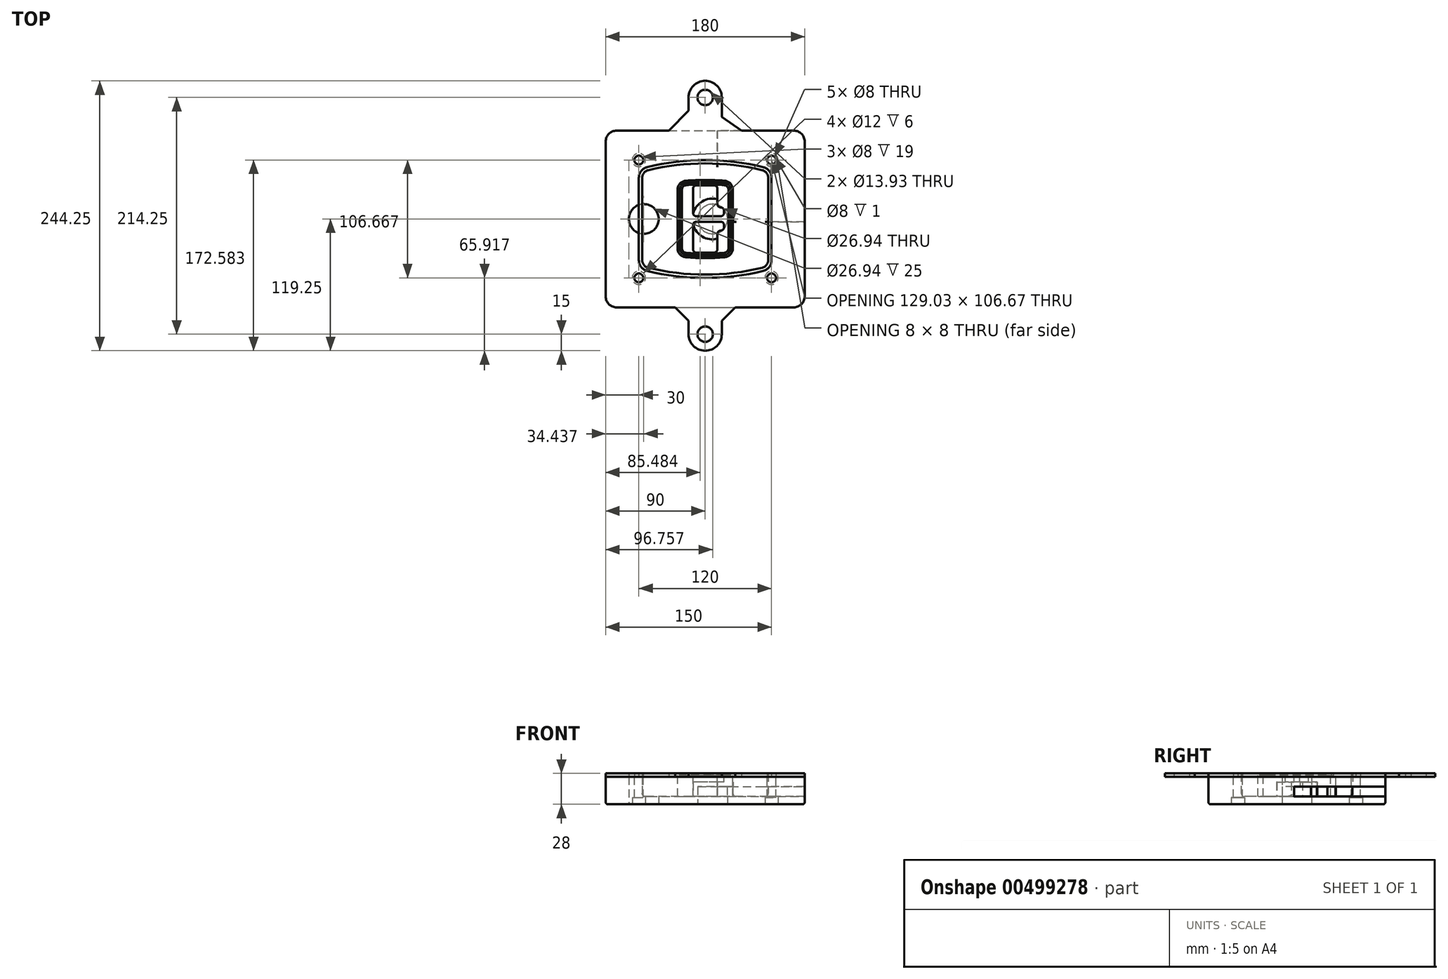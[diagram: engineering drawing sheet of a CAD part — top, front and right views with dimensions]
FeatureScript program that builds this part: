
annotation { "Feature Type Name" : "Feature", "Feature Type Description" : "" }
export const myFeature = defineFeature(function(context is Context, id is Id, definition is map)
    precondition{}
    {
        {
            var Q0;
            Q0=qCreatedBy(makeId("Top.planeOp"),FACE);
            var sketch = newSketch(context, id + "F0", { "sketchPlane" : qUnion([Q0])});
            skPoint(sketch, "E0.rect.middle", {"position": v(0, 0) * mm});
            skLineSegment(sketch, "E1.bottom", {"start": v(-80, -80) * mm, "end": v(80, -80) * mm});
            skLineSegment(sketch, "E1.top", {"start": v(-80, 80) * mm, "end": v(80, 80) * mm});
            skLineSegment(sketch, "E1.left", {"start": v(-90, -70) * mm, "end": v(-90, 70) * mm});
            skLineSegment(sketch, "E1.right", {"start": v(90, -70) * mm, "end": v(90, 70) * mm});
            skLineSegment(sketch, "E2", {"start": v(-90, 80) * mm, "end": v(90, -80) * mm, "construction": true});
            skLineSegment(sketch, "E3", {"start": v(90, 80) * mm, "end": v(-90, -80) * mm, "construction": true});
            skCircle(sketch, "E4", {"center": v(-60, 53.33) * mm, "radius": 4 * mm});
            skCircle(sketch, "E5", {"center": v(60, 53.33) * mm, "radius": 4 * mm});
            skCircle(sketch, "E6", {"center": v(60, -53.33) * mm, "radius": 4 * mm});
            skCircle(sketch, "E7", {"center": v(-60, -53.33) * mm, "radius": 4 * mm});
            skLineSegment(sketch, "E8", {"start": v(-60, 53.33) * mm, "end": v(60, 53.33) * mm, "construction": true});
            skLineSegment(sketch, "E9", {"start": v(60, 53.33) * mm, "end": v(60, -53.33) * mm, "construction": true});
            skLineSegment(sketch, "E10", {"start": v(60, -53.33) * mm, "end": v(-60, -53.33) * mm, "construction": true});
            skLineSegment(sketch, "E11", {"start": v(-60, -53.33) * mm, "end": v(-60, 53.33) * mm, "construction": true});
            skLineSegment(sketch, "E12", {"start": v(-60, 37.3) * mm, "end": v(-60, -37.3) * mm});
            skLineSegment(sketch, "E13", {"start": v(60, 37.3) * mm, "end": v(60, -37.3) * mm});
            skArc(sketch, "E14", {"start": v(52.38, 47.01) * mm, "mid": v(0, 53.33) * mm, "end": v(-52.38, 47.01) * mm});
            skArc(sketch, "E15", {"start": v(-52.38, -47.01) * mm, "mid": v(0, -53.33) * mm, "end": v(52.38, -47.01) * mm});
            skLineSegment(sketch, "E16", {"start": v(-60, 0) * mm, "end": v(60, 0) * mm, "construction": true});
            skPoint(sketch, "E17.visualSharp", {"position": v(-60, -45) * mm});
            skArc(sketch, "E17.filletArc", {"start": v(-60, -37.3) * mm, "mid": v(-57.87, -43.47) * mm, "end": v(-52.38, -47.01) * mm});
            skPoint(sketch, "E18.visualSharp", {"position": v(-60, 45) * mm});
            skArc(sketch, "E18.filletArc", {"start": v(-52.38, 47.01) * mm, "mid": v(-57.87, 43.47) * mm, "end": v(-60, 37.3) * mm});
            skPoint(sketch, "E19.visualSharp", {"position": v(60, 45) * mm});
            skArc(sketch, "E19.filletArc", {"start": v(60, 37.3) * mm, "mid": v(57.87, 43.47) * mm, "end": v(52.38, 47.01) * mm});
            skPoint(sketch, "E20.visualSharp", {"position": v(60, -45) * mm});
            skArc(sketch, "E20.filletArc", {"start": v(52.38, -47.01) * mm, "mid": v(57.87, -43.47) * mm, "end": v(60, -37.3) * mm});
            skPoint(sketch, "E21.visualSharp", {"position": v(-90, 80) * mm});
            skArc(sketch, "E21.filletArc", {"start": v(-80, 80) * mm, "mid": v(-87.07, 77.07) * mm, "end": v(-90, 70) * mm});
            skPoint(sketch, "E22.visualSharp", {"position": v(90, 80) * mm});
            skArc(sketch, "E22.filletArc", {"start": v(90, 70) * mm, "mid": v(87.07, 77.07) * mm, "end": v(80, 80) * mm});
            skPoint(sketch, "E23.visualSharp", {"position": v(90, -80) * mm});
            skArc(sketch, "E23.filletArc", {"start": v(80, -80) * mm, "mid": v(87.07, -77.07) * mm, "end": v(90, -70) * mm});
            skPoint(sketch, "E24.visualSharp", {"position": v(-90, -80) * mm});
            skArc(sketch, "E24.filletArc", {"start": v(-90, -70) * mm, "mid": v(-87.07, -77.07) * mm, "end": v(-80, -80) * mm});
            skArc(sketch, "E25.0", {"start": v(57, 37.3) * mm, "mid": v(55.5, 41.62) * mm, "end": v(51.67, 44.1) * mm});
            skLineSegment(sketch, "E25.1", {"start": v(57, 37.3) * mm, "end": v(57, -37.3) * mm});
            skArc(sketch, "E25.2", {"start": v(51.67, -44.1) * mm, "mid": v(55.5, -41.62) * mm, "end": v(57, -37.3) * mm});
            skArc(sketch, "E25.3", {"start": v(-51.67, -44.1) * mm, "mid": v(0, -50.33) * mm, "end": v(51.67, -44.1) * mm});
            skArc(sketch, "E25.4", {"start": v(-57, -37.3) * mm, "mid": v(-55.5, -41.62) * mm, "end": v(-51.67, -44.1) * mm});
            skArc(sketch, "E25.5", {"start": v(51.67, 44.1) * mm, "mid": v(0, 50.33) * mm, "end": v(-51.67, 44.1) * mm});
            skLineSegment(sketch, "E25.6", {"start": v(-57, 37.3) * mm, "end": v(-57, -37.3) * mm});
            skArc(sketch, "E25.7", {"start": v(-51.67, 44.1) * mm, "mid": v(-55.5, 41.62) * mm, "end": v(-57, 37.3) * mm});
            skArc(sketch, "E26.0", {"start": v(-53.33, 50.9) * mm, "mid": v(-61.01, 45.94) * mm, "end": v(-64, 37.3) * mm});
            skArc(sketch, "E26.1", {"start": v(53.33, 50.9) * mm, "mid": v(0, 57.33) * mm, "end": v(-53.33, 50.9) * mm});
            skArc(sketch, "E26.2", {"start": v(64, 37.3) * mm, "mid": v(61.01, 45.94) * mm, "end": v(53.33, 50.9) * mm});
            skLineSegment(sketch, "E26.3", {"start": v(64, 37.3) * mm, "end": v(64, -37.3) * mm});
            skArc(sketch, "E26.4", {"start": v(53.33, -50.9) * mm, "mid": v(61.01, -45.94) * mm, "end": v(64, -37.3) * mm});
            skLineSegment(sketch, "E26.5", {"start": v(-64, 37.3) * mm, "end": v(-64, -37.3) * mm});
            skArc(sketch, "E26.6", {"start": v(-53.33, -50.9) * mm, "mid": v(0, -57.33) * mm, "end": v(53.33, -50.9) * mm});
            skArc(sketch, "E26.7", {"start": v(-64, -37.3) * mm, "mid": v(-61.01, -45.94) * mm, "end": v(-53.33, -50.9) * mm});
            skSolve(sketch);
        }
        {
            var Q0;
            Q0=makeQuery(id+"F0.imprint","IMPRINT",FACE,{"disambiguationData":[TD([[makeQuery(id+"F0.imprint","IMPRINT",EDGE,{"derivedFrom":sQuery(id+"F0.wireOp",EDGE,"E1.bottom")}),1.0]])]});
            var Q1;
            Q1=makeQuery(id+"F0.imprint","IMPRINT",FACE,{"disambiguationData":[TD([[makeQuery(id+"F0.imprint","IMPRINT",EDGE,{"derivedFrom":sQuery(id+"F0.wireOp",EDGE,"E12")}),1.0]])]});
            var Q2;
            Q2=makeQuery(id+"F0.imprint","IMPRINT",FACE,{"disambiguationData":[TD([[makeQuery(id+"F0.imprint","IMPRINT",EDGE,{"derivedFrom":sQuery(id+"F0.wireOp",EDGE,"E25.0")}),1.0]])]});
            var Q3;
            Q3=makeQuery(id+"F0.imprint","IMPRINT",FACE,{"disambiguationData":[TD([[makeQuery(id+"F0.imprint","IMPRINT",EDGE,{"derivedFrom":sQuery(id+"F0.wireOp",EDGE,"E12")}),-1.0]])]});
            extrude(context, id + "F1", {"entities" : qUnion([Q0, Q1, Q2, Q3]), "oppositeDirection" : true, "depth" : 25 * mm});
        }
        {
            var Q0;
            Q0=makeQuery(id+"F0.imprint","IMPRINT",FACE,{"disambiguationData":[TD([[makeQuery(id+"F0.imprint","IMPRINT",EDGE,{"derivedFrom":sQuery(id+"F0.wireOp",EDGE,"E12")}),1.0]])]});
            extrude(context, id + "F2", {"entities" : qUnion([Q0]), "operationType" : NewBodyOperationType.ADD, "depth" : 3 * mm});
        }
        {
            var Q0;
            Q0=makeQuery(id+"F0.imprint","IMPRINT",FACE,{"disambiguationData":[TD([[makeQuery(id+"F0.imprint","IMPRINT",EDGE,{"derivedFrom":sQuery(id+"F0.wireOp",EDGE,"E25.0")}),1.0]])]});
            extrude(context, id + "F3", {"entities" : qUnion([Q0]), "operationType" : NewBodyOperationType.REMOVE, "oppositeDirection" : true, "depth" : 18 * mm});
        }
        {
            var Q0;
            Q0=makeQuery(id+"F2.opExtrude","CAP_FACE",FACE,{"disambiguationData":[OSD([sQuery(id+"F0.wireOp",EDGE,"E12"),sQuery(id+"F0.wireOp",EDGE,"E13"),sQuery(id+"F0.wireOp",EDGE,"E14"),sQuery(id+"F0.wireOp",EDGE,"E15"),sQuery(id+"F0.wireOp",EDGE,"E17.filletArc"),sQuery(id+"F0.wireOp",EDGE,"E18.filletArc"),sQuery(id+"F0.wireOp",EDGE,"E19.filletArc"),sQuery(id+"F0.wireOp",EDGE,"E20.filletArc"),sQuery(id+"F0.wireOp",EDGE,"E25.0"),sQuery(id+"F0.wireOp",EDGE,"E25.1"),sQuery(id+"F0.wireOp",EDGE,"E25.2"),sQuery(id+"F0.wireOp",EDGE,"E25.3"),sQuery(id+"F0.wireOp",EDGE,"E25.4"),sQuery(id+"F0.wireOp",EDGE,"E25.5"),sQuery(id+"F0.wireOp",EDGE,"E25.6"),sQuery(id+"F0.wireOp",EDGE,"E25.7")])],"isStart":false});
            var sketch = newSketch(context, id + "F4", { "sketchPlane" : qUnion([Q0])});
            skArc(sketch, "E27.0", {"start": v(-17.7, -34.56) * mm, "mid": v(0, -35.33) * mm, "end": v(17.7, -34.56) * mm});
            skArc(sketch, "E28.0", {"start": v(17.7, 34.56) * mm, "mid": v(0, 35.33) * mm, "end": v(-17.7, 34.56) * mm});
            skLineSegment(sketch, "E29", {"start": v(-25, 26.59) * mm, "end": v(-25, -26.59) * mm});
            skLineSegment(sketch, "E30", {"start": v(25, 26.59) * mm, "end": v(25, -26.59) * mm});
            skLineSegment(sketch, "E31", {"start": v(-25, 33.78) * mm, "end": v(25, 33.78) * mm, "construction": true});
            skLineSegment(sketch, "E32", {"start": v(-25, -33.78) * mm, "end": v(25, -33.78) * mm, "construction": true});
            skPoint(sketch, "E33.visualSharp", {"position": v(-25, 33.78) * mm});
            skArc(sketch, "E33.filletArc", {"start": v(-17.7, 34.56) * mm, "mid": v(-22.9, 32) * mm, "end": v(-25, 26.59) * mm});
            skPoint(sketch, "E34.visualSharp", {"position": v(25, 33.78) * mm});
            skArc(sketch, "E34.filletArc", {"start": v(25, 26.59) * mm, "mid": v(22.9, 32) * mm, "end": v(17.7, 34.56) * mm});
            skPoint(sketch, "E35.visualSharp", {"position": v(25, -33.78) * mm});
            skArc(sketch, "E35.filletArc", {"start": v(17.7, -34.56) * mm, "mid": v(22.9, -32) * mm, "end": v(25, -26.59) * mm});
            skPoint(sketch, "E36.visualSharp", {"position": v(-25, -33.78) * mm});
            skArc(sketch, "E36.filletArc", {"start": v(-25, -26.59) * mm, "mid": v(-22.9, -32) * mm, "end": v(-17.7, -34.56) * mm});
            skArc(sketch, "E37.0", {"start": v(51.67, 44.1) * mm, "mid": v(0, 50.33) * mm, "end": v(-51.67, 44.1) * mm});
            skArc(sketch, "E37.1", {"start": v(-51.67, 44.1) * mm, "mid": v(-55.5, 41.62) * mm, "end": v(-57, 37.3) * mm});
            skLineSegment(sketch, "E37.2", {"start": v(-57, 37.3) * mm, "end": v(-57, -37.3) * mm});
            skArc(sketch, "E37.3", {"start": v(-57, -37.3) * mm, "mid": v(-55.5, -41.62) * mm, "end": v(-51.67, -44.1) * mm});
            skArc(sketch, "E37.4", {"start": v(-51.67, -44.1) * mm, "mid": v(0, -50.33) * mm, "end": v(51.67, -44.1) * mm});
            skArc(sketch, "E37.5", {"start": v(51.67, -44.1) * mm, "mid": v(55.5, -41.62) * mm, "end": v(57, -37.3) * mm});
            skLineSegment(sketch, "E37.6", {"start": v(57, 37.3) * mm, "end": v(57, -37.3) * mm});
            skArc(sketch, "E37.7", {"start": v(57, 37.3) * mm, "mid": v(55.5, 41.62) * mm, "end": v(51.67, 44.1) * mm});
            skLineSegment(sketch, "E38.0", {"start": v(23, 26.59) * mm, "end": v(23, -26.59) * mm});
            skArc(sketch, "E38.1", {"start": v(17.53, -32.56) * mm, "mid": v(21.42, -30.64) * mm, "end": v(23, -26.59) * mm});
            skArc(sketch, "E38.2", {"start": v(-17.53, -32.56) * mm, "mid": v(0, -33.33) * mm, "end": v(17.53, -32.56) * mm});
            skArc(sketch, "E38.3", {"start": v(-23, -26.59) * mm, "mid": v(-21.42, -30.64) * mm, "end": v(-17.53, -32.56) * mm});
            skLineSegment(sketch, "E38.4", {"start": v(-23, 26.59) * mm, "end": v(-23, -26.59) * mm});
            skArc(sketch, "E38.5", {"start": v(23, 26.59) * mm, "mid": v(21.42, 30.64) * mm, "end": v(17.53, 32.56) * mm});
            skArc(sketch, "E38.6", {"start": v(-17.53, 32.56) * mm, "mid": v(-21.42, 30.64) * mm, "end": v(-23, 26.59) * mm});
            skArc(sketch, "E38.7", {"start": v(17.53, 32.56) * mm, "mid": v(0, 33.33) * mm, "end": v(-17.53, 32.56) * mm});
            skArc(sketch, "E39.0", {"start": v(21, 26.59) * mm, "mid": v(19.95, 29.29) * mm, "end": v(17.35, 30.57) * mm});
            skLineSegment(sketch, "E39.1", {"start": v(21, 26.59) * mm, "end": v(21, -26.59) * mm});
            skArc(sketch, "E39.2", {"start": v(17.35, -30.57) * mm, "mid": v(19.95, -29.29) * mm, "end": v(21, -26.59) * mm});
            skArc(sketch, "E39.3", {"start": v(-17.35, -30.57) * mm, "mid": v(0, -31.33) * mm, "end": v(17.35, -30.57) * mm});
            skArc(sketch, "E39.4", {"start": v(-21, -26.59) * mm, "mid": v(-19.95, -29.29) * mm, "end": v(-17.35, -30.57) * mm});
            skArc(sketch, "E39.5", {"start": v(17.35, 30.57) * mm, "mid": v(0, 31.33) * mm, "end": v(-17.35, 30.57) * mm});
            skLineSegment(sketch, "E39.6", {"start": v(-21, 26.59) * mm, "end": v(-21, -26.59) * mm});
            skArc(sketch, "E39.7", {"start": v(-17.35, 30.57) * mm, "mid": v(-19.95, 29.29) * mm, "end": v(-21, 26.59) * mm});
            skLineSegment(sketch, "E40", {"start": v(-25, 0) * mm, "end": v(25, 0) * mm, "construction": true});
            skLineSegment(sketch, "E41", {"start": v(-11, 5.5) * mm, "end": v(-11, 27.5) * mm});
            skLineSegment(sketch, "E42", {"start": v(-8, 30.5) * mm, "end": v(8, 30.5) * mm});
            skLineSegment(sketch, "E43", {"start": v(11, 27.5) * mm, "end": v(11, 13.5) * mm});
            skLineSegment(sketch, "E44", {"start": v(14, 10.5) * mm, "end": v(14, 10.5) * mm});
            skLineSegment(sketch, "E45", {"start": v(17, 7.5) * mm, "end": v(17, 5.5) * mm});
            skLineSegment(sketch, "E46", {"start": v(14, 2.5) * mm, "end": v(-8, 2.5) * mm});
            skPoint(sketch, "E47.visualSharp", {"position": v(-11, 30.5) * mm});
            skArc(sketch, "E47.filletArc", {"start": v(-8, 30.5) * mm, "mid": v(-10.12, 29.62) * mm, "end": v(-11, 27.5) * mm});
            skPoint(sketch, "E48.visualSharp", {"position": v(11, 30.5) * mm});
            skArc(sketch, "E48.filletArc", {"start": v(11, 27.5) * mm, "mid": v(10.12, 29.62) * mm, "end": v(8, 30.5) * mm});
            skPoint(sketch, "E49.visualSharp", {"position": v(11, 10.5) * mm});
            skArc(sketch, "E49.filletArc", {"start": v(11, 13.5) * mm, "mid": v(11.88, 11.38) * mm, "end": v(14, 10.5) * mm});
            skPoint(sketch, "E50.visualSharp", {"position": v(17, 10.5) * mm});
            skArc(sketch, "E50.filletArc", {"start": v(17, 7.5) * mm, "mid": v(16.12, 9.62) * mm, "end": v(14, 10.5) * mm});
            skPoint(sketch, "E51.visualSharp", {"position": v(17, 2.5) * mm});
            skArc(sketch, "E51.filletArc", {"start": v(14, 2.5) * mm, "mid": v(16.12, 3.38) * mm, "end": v(17, 5.5) * mm});
            skPoint(sketch, "E52.visualSharp", {"position": v(-11, 2.5) * mm});
            skArc(sketch, "E52.filletArc", {"start": v(-11, 5.5) * mm, "mid": v(-10.12, 3.38) * mm, "end": v(-8, 2.5) * mm});
            skLineSegment(sketch, "E53.0.MirrorCS", {"start": v(14, -2.5) * mm, "end": v(-8, -2.5) * mm});
            skArc(sketch, "E54.0.MirrorCS", {"start": v(-11, -5.5) * mm, "mid": v(-10.12, -3.38) * mm, "end": v(-8, -2.5) * mm});
            skLineSegment(sketch, "E55.0.MirrorCS", {"start": v(-11, -5.5) * mm, "end": v(-11, -27.5) * mm});
            skArc(sketch, "E56.0.MirrorCS", {"start": v(-8, -30.5) * mm, "mid": v(-10.12, -29.62) * mm, "end": v(-11, -27.5) * mm});
            skLineSegment(sketch, "E57.0.MirrorCS", {"start": v(-8, -30.5) * mm, "end": v(8, -30.5) * mm});
            skArc(sketch, "E58.0.MirrorCS", {"start": v(11, -27.5) * mm, "mid": v(10.12, -29.62) * mm, "end": v(8, -30.5) * mm});
            skLineSegment(sketch, "E59.0.MirrorCS", {"start": v(11, -27.5) * mm, "end": v(11, -13.5) * mm});
            skArc(sketch, "E60.0.MirrorCS", {"start": v(11, -13.5) * mm, "mid": v(11.88, -11.38) * mm, "end": v(14, -10.5) * mm});
            skArc(sketch, "E61.0.MirrorCS", {"start": v(17, -7.5) * mm, "mid": v(16.12, -9.62) * mm, "end": v(14, -10.5) * mm});
            skLineSegment(sketch, "E62.0.MirrorCS", {"start": v(17, -7.5) * mm, "end": v(17, -5.5) * mm});
            skArc(sketch, "E63.0.MirrorCS", {"start": v(14, -2.5) * mm, "mid": v(16.12, -3.38) * mm, "end": v(17, -5.5) * mm});
            skSolve(sketch);
        }
        {
            var Q0;
            Q0=makeQuery(id+"F4.imprint","IMPRINT",FACE,{"disambiguationData":[TD([[makeQuery(id+"F4.imprint","IMPRINT",EDGE,{"derivedFrom":sQuery(id+"F4.wireOp",EDGE,"E27.0")}),1.0]])]});
            var Q1;
            Q1=makeQuery(id+"F4.imprint","IMPRINT",FACE,{"disambiguationData":[TD([[makeQuery(id+"F4.imprint","IMPRINT",EDGE,{"derivedFrom":sQuery(id+"F4.wireOp",EDGE,"E38.0")}),-1.0]])]});
            var Q2;
            Q2=makeQuery(id+"F4.imprint","IMPRINT",FACE,{"disambiguationData":[TD([[makeQuery(id+"F4.imprint","IMPRINT",EDGE,{"derivedFrom":sQuery(id+"F4.wireOp",EDGE,"E39.0")}),1.0]])]});
            extrude(context, id + "F5", {"entities" : qUnion([Q0, Q1, Q2]), "operationType" : NewBodyOperationType.ADD, "endBound" : BoundingType.UP_TO_NEXT, "oppositeDirection" : true, "depth" : 25 * mm});
        }
        {
            var Q0;
            Q0=makeQuery(id+"F4.imprint","IMPRINT",FACE,{"disambiguationData":[TD([[makeQuery(id+"F4.imprint","IMPRINT",EDGE,{"derivedFrom":sQuery(id+"F4.wireOp",EDGE,"E38.0")}),-1.0]])]});
            extrude(context, id + "F6", {"entities" : qUnion([Q0]), "operationType" : NewBodyOperationType.REMOVE, "oppositeDirection" : true, "depth" : 2 * mm});
        }
        {
            var Q0;
            Q0=makeQuery(id+"F1.opExtrude","CAP_FACE",FACE,{"disambiguationData":[OSD([sQuery(id+"F0.wireOp",EDGE,"E1.bottom"),sQuery(id+"F0.wireOp",EDGE,"E1.top"),sQuery(id+"F0.wireOp",EDGE,"E1.left"),sQuery(id+"F0.wireOp",EDGE,"E1.right"),sQuery(id+"F0.wireOp",EDGE,"E4"),sQuery(id+"F0.wireOp",EDGE,"E5"),sQuery(id+"F0.wireOp",EDGE,"E6"),sQuery(id+"F0.wireOp",EDGE,"E7"),sQuery(id+"F0.wireOp",EDGE,"E21.filletArc"),sQuery(id+"F0.wireOp",EDGE,"E22.filletArc"),sQuery(id+"F0.wireOp",EDGE,"E23.filletArc"),sQuery(id+"F0.wireOp",EDGE,"E24.filletArc")])],"isStart":false});
            var sketch = newSketch(context, id + "F7", { "sketchPlane" : qUnion([Q0])});
            skCircle(sketch, "E64", {"center": v(6.76, 0) * mm, "radius": 13.47 * mm});
            skCircle(sketch, "E65", {"center": v(-55.56, 0) * mm, "radius": 13.47 * mm});
            skLineSegment(sketch, "E66", {"start": v(90, 0) * mm, "end": v(-90, 0) * mm});
            skCircle(sketch, "E67", {"center": v(6.76, 0) * mm, "radius": 18.47 * mm});
            skCircle(sketch, "E68", {"center": v(60, -53.33) * mm, "radius": 6 * mm});
            skCircle(sketch, "E69", {"center": v(-60, -53.33) * mm, "radius": 6 * mm});
            skCircle(sketch, "E70", {"center": v(-60, 53.33) * mm, "radius": 6 * mm});
            skCircle(sketch, "E71", {"center": v(60, 53.33) * mm, "radius": 6 * mm});
            skSolve(sketch);
        }
        {
            var Q0;
            {var subQ1=sQuery(id+"F7.wireOp",EDGE,"E66");var subQ4=sQuery(id+"F7.wireOp",EDGE,"E64");var subQ6=makeQuery(id+"F7.imprint","INTERSECT",VERTEX,{"disambiguationData":[OD(0.0)],"derivedFrom":[subQ4,subQ1]});Q0=makeQuery(id+"F7.imprint","IMPRINT",FACE,{"disambiguationData":[TD([[makeQuery(id+"F7.imprint","IMPRINT",EDGE,{"disambiguationData":[TD([[subQ6,-1.0]])],"derivedFrom":subQ4}),-1.0]])]});}
            var Q1;
            {var subQ0=sQuery(id+"F7.wireOp",EDGE,"E66");var subQ1=sQuery(id+"F7.wireOp",EDGE,"E64");var subQ3=makeQuery(id+"F7.imprint","INTERSECT",VERTEX,{"disambiguationData":[OD(0.0)],"derivedFrom":[subQ1,subQ0]});Q1=makeQuery(id+"F7.imprint","IMPRINT",FACE,{"disambiguationData":[TD([[makeQuery(id+"F7.imprint","IMPRINT",EDGE,{"disambiguationData":[TD([[subQ3,-1.0]])],"derivedFrom":subQ1}),1.0]])]});}
            var Q2;
            {var subQ0=sQuery(id+"F7.wireOp",EDGE,"E66");var subQ1=sQuery(id+"F7.wireOp",EDGE,"E64");var subQ3=makeQuery(id+"F7.imprint","INTERSECT",VERTEX,{"disambiguationData":[OD(0.0)],"derivedFrom":[subQ1,subQ0]});Q2=makeQuery(id+"F7.imprint","IMPRINT",FACE,{"disambiguationData":[TD([[makeQuery(id+"F7.imprint","IMPRINT",EDGE,{"disambiguationData":[TD([[subQ3,1.0]])],"derivedFrom":subQ1}),1.0]])]});}
            var Q3;
            {var subQ1=sQuery(id+"F7.wireOp",EDGE,"E66");var subQ4=sQuery(id+"F7.wireOp",EDGE,"E64");var subQ6=makeQuery(id+"F7.imprint","INTERSECT",VERTEX,{"disambiguationData":[OD(0.0)],"derivedFrom":[subQ4,subQ1]});Q3=makeQuery(id+"F7.imprint","IMPRINT",FACE,{"disambiguationData":[TD([[makeQuery(id+"F7.imprint","IMPRINT",EDGE,{"disambiguationData":[TD([[subQ6,1.0]])],"derivedFrom":subQ4}),-1.0]])]});}
            extrude(context, id + "F8", {"entities" : qUnion([Q0, Q1, Q2, Q3]), "operationType" : NewBodyOperationType.ADD, "oppositeDirection" : true, "depth" : 20 * mm});
        }
        {
            var Q0;
            {var subQ0=sQuery(id+"F7.wireOp",EDGE,"E66");var subQ1=sQuery(id+"F7.wireOp",EDGE,"E64");var subQ3=makeQuery(id+"F7.imprint","INTERSECT",VERTEX,{"disambiguationData":[OD(0.0)],"derivedFrom":[subQ1,subQ0]});Q0=makeQuery(id+"F7.imprint","IMPRINT",FACE,{"disambiguationData":[TD([[makeQuery(id+"F7.imprint","IMPRINT",EDGE,{"disambiguationData":[TD([[subQ3,-1.0]])],"derivedFrom":subQ1}),1.0]])]});}
            var Q1;
            {var subQ0=sQuery(id+"F7.wireOp",EDGE,"E66");var subQ1=sQuery(id+"F7.wireOp",EDGE,"E64");var subQ3=makeQuery(id+"F7.imprint","INTERSECT",VERTEX,{"disambiguationData":[OD(0.0)],"derivedFrom":[subQ1,subQ0]});Q1=makeQuery(id+"F7.imprint","IMPRINT",FACE,{"disambiguationData":[TD([[makeQuery(id+"F7.imprint","IMPRINT",EDGE,{"disambiguationData":[TD([[subQ3,1.0]])],"derivedFrom":subQ1}),1.0]])]});}
            extrude(context, id + "F9", {"entities" : qUnion([Q0, Q1]), "operationType" : NewBodyOperationType.REMOVE, "oppositeDirection" : true, "depth" : 16 * mm});
        }
        {
            var Q0;
            {var subQ0=sQuery(id+"F7.wireOp",EDGE,"E66");var subQ1=sQuery(id+"F7.wireOp",EDGE,"E65");var subQ3=makeQuery(id+"F7.imprint","INTERSECT",VERTEX,{"disambiguationData":[OD(0.0)],"derivedFrom":[subQ1,subQ0]});Q0=makeQuery(id+"F7.imprint","IMPRINT",FACE,{"disambiguationData":[TD([[makeQuery(id+"F7.imprint","IMPRINT",EDGE,{"disambiguationData":[TD([[subQ3,-1.0]])],"derivedFrom":subQ1}),1.0]])]});}
            var Q1;
            {var subQ0=sQuery(id+"F7.wireOp",EDGE,"E66");var subQ1=sQuery(id+"F7.wireOp",EDGE,"E65");var subQ3=makeQuery(id+"F7.imprint","INTERSECT",VERTEX,{"disambiguationData":[OD(0.0)],"derivedFrom":[subQ1,subQ0]});Q1=makeQuery(id+"F7.imprint","IMPRINT",FACE,{"disambiguationData":[TD([[makeQuery(id+"F7.imprint","IMPRINT",EDGE,{"disambiguationData":[TD([[subQ3,1.0]])],"derivedFrom":subQ1}),1.0]])]});}
            extrude(context, id + "F10", {"entities" : qUnion([Q0, Q1]), "operationType" : NewBodyOperationType.REMOVE, "oppositeDirection" : true, "depth" : 25 * mm});
        }
        {
            var Q0;
            Q0=makeQuery(id+"F7.imprint","IMPRINT",FACE,{"disambiguationData":[TD([[makeQuery(id+"F7.imprint","IMPRINT",EDGE,{"derivedFrom":sQuery(id+"F7.wireOp",EDGE,"E68")}),1.0]])]});
            var Q1;
            Q1=makeQuery(id+"F7.imprint","IMPRINT",FACE,{"disambiguationData":[TD([[makeQuery(id+"F7.imprint","IMPRINT",EDGE,{"derivedFrom":makeQuery(id+"F1.opExtrude","CAP_EDGE",EDGE,{"disambiguationData":[OSD([sQuery(id+"F0.wireOp",EDGE,"E5")])],"isStart":false})}),-1.0]])]});
            var Q2;
            Q2=makeQuery(id+"F7.imprint","IMPRINT",FACE,{"disambiguationData":[TD([[makeQuery(id+"F7.imprint","IMPRINT",EDGE,{"derivedFrom":sQuery(id+"F7.wireOp",EDGE,"E69")}),1.0]])]});
            var Q3;
            Q3=makeQuery(id+"F7.imprint","IMPRINT",FACE,{"disambiguationData":[TD([[makeQuery(id+"F7.imprint","IMPRINT",EDGE,{"derivedFrom":makeQuery(id+"F1.opExtrude","CAP_EDGE",EDGE,{"disambiguationData":[OSD([sQuery(id+"F0.wireOp",EDGE,"E4")])],"isStart":false})}),-1.0]])]});
            var Q4;
            Q4=makeQuery(id+"F7.imprint","IMPRINT",FACE,{"disambiguationData":[TD([[makeQuery(id+"F7.imprint","IMPRINT",EDGE,{"derivedFrom":sQuery(id+"F7.wireOp",EDGE,"E70")}),1.0]])]});
            var Q5;
            Q5=makeQuery(id+"F7.imprint","IMPRINT",FACE,{"disambiguationData":[TD([[makeQuery(id+"F7.imprint","IMPRINT",EDGE,{"derivedFrom":makeQuery(id+"F1.opExtrude","CAP_EDGE",EDGE,{"disambiguationData":[OSD([sQuery(id+"F0.wireOp",EDGE,"E7")])],"isStart":false})}),-1.0]])]});
            var Q6;
            Q6=makeQuery(id+"F7.imprint","IMPRINT",FACE,{"disambiguationData":[TD([[makeQuery(id+"F7.imprint","IMPRINT",EDGE,{"derivedFrom":sQuery(id+"F7.wireOp",EDGE,"E71")}),1.0]])]});
            var Q7;
            Q7=makeQuery(id+"F7.imprint","IMPRINT",FACE,{"disambiguationData":[TD([[makeQuery(id+"F7.imprint","IMPRINT",EDGE,{"derivedFrom":makeQuery(id+"F1.opExtrude","CAP_EDGE",EDGE,{"disambiguationData":[OSD([sQuery(id+"F0.wireOp",EDGE,"E6")])],"isStart":false})}),-1.0]])]});
            extrude(context, id + "F11", {"entities" : qUnion([Q0, Q1, Q2, Q3, Q4, Q5, Q6, Q7]), "operationType" : NewBodyOperationType.REMOVE, "oppositeDirection" : true, "depth" : 6 * mm});
        }
        {
            var Q0;
            Q0=makeQuery(id+"F9.boolean.opBoolean","COPY",FACE,{"derivedFrom":makeQuery(id+"F9.opExtrude","CAP_FACE",FACE,{"disambiguationData":[OSD([sQuery(id+"F7.wireOp",EDGE,"E64")])],"isStart":false})});
            var sketch = newSketch(context, id + "F12", { "sketchPlane" : qUnion([Q0])});
            skArc(sketch, "E72.0", {"start": v(11, -88.19) * mm, "mid": v(97.1, -83.6) * mm, "end": v(92.5, 2.5) * mm});
            skLineSegment(sketch, "E72.1", {"start": v(11, -17.97) * mm, "end": v(11, -17.97) * mm});
            skLineSegment(sketch, "E73", {"start": v(92.5, -105.13) * mm, "end": v(102.3, -105.13) * mm});
            skLineSegment(sketch, "E74.0", {"start": v(92.5, 2.5) * mm, "end": v(14, 2.5) * mm});
            skArc(sketch, "E74.1", {"start": v(14, 2.5) * mm, "mid": v(16.12, 3.38) * mm, "end": v(17, 5.5) * mm});
            skLineSegment(sketch, "E74.2", {"start": v(17, 7.5) * mm, "end": v(17, 5.5) * mm});
            skArc(sketch, "E74.3", {"start": v(17, 7.5) * mm, "mid": v(16.12, 9.62) * mm, "end": v(14, 10.5) * mm});
            skArc(sketch, "E74.4", {"start": v(11, 13.5) * mm, "mid": v(11.88, 11.38) * mm, "end": v(14, 10.5) * mm});
            skLineSegment(sketch, "E74.5", {"start": v(11, 13.5) * mm, "end": v(11, -88.19) * mm});
            skLineSegment(sketch, "E74.7", {"start": v(92.5, -2.5) * mm, "end": v(14, -2.5) * mm});
            skArc(sketch, "E74.8", {"start": v(14, -2.5) * mm, "mid": v(16.12, -3.38) * mm, "end": v(17, -5.5) * mm});
            skLineSegment(sketch, "E74.9", {"start": v(17, -7.5) * mm, "end": v(17, -5.5) * mm});
            skArc(sketch, "E74.10", {"start": v(17, -7.5) * mm, "mid": v(16.12, -9.62) * mm, "end": v(14, -10.5) * mm});
            skArc(sketch, "E74.11", {"start": v(11, -13.5) * mm, "mid": v(11.88, -11.38) * mm, "end": v(14, -10.5) * mm});
            skLineSegment(sketch, "E74.12", {"start": v(11, -17.97) * mm, "end": v(11, -13.5) * mm});
            skPoint(sketch, "E75.orphan", {"position": v(11, -27.5) * mm});
            skPoint(sketch, "E76.orphan", {"position": v(-8, -2.5) * mm});
            skPoint(sketch, "E77.orphan", {"position": v(-8, 2.5) * mm});
            skPoint(sketch, "E78.orphan", {"position": v(11, 27.5) * mm});
            skSolve(sketch);
        }
        {
            var Q0;
            {var subQ7=sQuery(id+"F12.wireOp",EDGE,"E72.0");var subQ14=sQuery(id+"F12.wireOp",EDGE,"E72.1");var subQ16=sQuery(id+"F12.wireOp",EDGE,"E74.1");var subQ18=sQuery(id+"F12.wireOp",EDGE,"E74.8");Q0=qUnion([makeQuery(id+"F12.imprint","IMPRINT",FACE,{"disambiguationData":[TD([[makeQuery(id+"F12.imprint","IMPRINT",EDGE,{"derivedFrom":subQ7}),1.0]])]}),makeQuery(id+"F12.imprint","IMPRINT",FACE,{"disambiguationData":[TD([[makeQuery(id+"F12.imprint","IMPRINT",EDGE,{"derivedFrom":subQ14}),1.0]])]}),makeQuery(id+"F12.imprint","IMPRINT",FACE,{"disambiguationData":[TD([[makeQuery(id+"F12.imprint","IMPRINT",EDGE,{"derivedFrom":subQ16}),1.0]])]}),makeQuery(id+"F12.imprint","IMPRINT",FACE,{"disambiguationData":[TD([[makeQuery(id+"F12.imprint","IMPRINT",EDGE,{"derivedFrom":subQ18}),-1.0]])]})]);}
            var Q1;
            Q1=makeQuery(id+"F5.boolean.opBoolean","SPLIT",FACE,{"disambiguationData":[TD([makeQuery(id+"F5.opExtrude","SWEPT_FACE",FACE,{"disambiguationData":[OSD([sQuery(id+"F4.wireOp",EDGE,"E41")])]})])],"derivedFrom":makeQuery(id+"F3.boolean.opBoolean","COPY",FACE,{"derivedFrom":makeQuery(id+"F3.opExtrude","CAP_FACE",FACE,{"disambiguationData":[OSD([sQuery(id+"F0.wireOp",EDGE,"E25.0"),sQuery(id+"F0.wireOp",EDGE,"E25.1"),sQuery(id+"F0.wireOp",EDGE,"E25.2"),sQuery(id+"F0.wireOp",EDGE,"E25.3"),sQuery(id+"F0.wireOp",EDGE,"E25.4"),sQuery(id+"F0.wireOp",EDGE,"E25.5"),sQuery(id+"F0.wireOp",EDGE,"E25.6"),sQuery(id+"F0.wireOp",EDGE,"E25.7")])],"isStart":false})})});
            extrude(context, id + "F13", {"entities" : qUnion([Q0]), "operationType" : NewBodyOperationType.REMOVE, "endBound" : BoundingType.UP_TO_SURFACE, "endBoundEntityFace" : qUnion([Q1]), "depth" : 25 * mm});
        }
        {
            var Q0;
            Q0=makeQuery(id+"F3.boolean.opBoolean","COPY",EDGE,{"derivedFrom":makeQuery(id+"F3.opExtrude","CAP_EDGE",EDGE,{"disambiguationData":[OSD([sQuery(id+"F0.wireOp",EDGE,"E25.6")])],"isStart":false})});
            var Q1;
            Q1=makeQuery(id+"F8.boolean.opBoolean","INTERSECT",EDGE,{"derivedFrom":[makeQuery(id+"F5.opExtrude","SWEPT_FACE",FACE,{"disambiguationData":[OSD([sQuery(id+"F4.wireOp",EDGE,"E30")])]}),makeQuery(id+"F8.opExtrude","CAP_FACE",FACE,{"disambiguationData":[OSD([sQuery(id+"F7.wireOp",EDGE,"E67")])],"isStart":false})]});
            var Q2;
            Q2=makeQuery(id+"F8.boolean.opBoolean","INTERSECT",EDGE,{"disambiguationData":[OD(1.0)],"derivedFrom":[makeQuery(id+"F5.opExtrude","SWEPT_FACE",FACE,{"disambiguationData":[OSD([sQuery(id+"F4.wireOp",EDGE,"E30")])]}),makeQuery(id+"F8.opExtrude","SWEPT_FACE",FACE,{"disambiguationData":[OSD([sQuery(id+"F7.wireOp",EDGE,"E67")])]})]});
            var Q3;
            {var subQ0=makeQuery(id+"F3.boolean.opBoolean","COPY",FACE,{"derivedFrom":makeQuery(id+"F3.opExtrude","CAP_FACE",FACE,{"disambiguationData":[OSD([sQuery(id+"F0.wireOp",EDGE,"E25.0"),sQuery(id+"F0.wireOp",EDGE,"E25.1"),sQuery(id+"F0.wireOp",EDGE,"E25.2"),sQuery(id+"F0.wireOp",EDGE,"E25.3"),sQuery(id+"F0.wireOp",EDGE,"E25.4"),sQuery(id+"F0.wireOp",EDGE,"E25.5"),sQuery(id+"F0.wireOp",EDGE,"E25.6"),sQuery(id+"F0.wireOp",EDGE,"E25.7")])],"isStart":false})});var subQ1=sQuery(id+"F4.wireOp",EDGE,"E30");Q3=makeQuery(id+"F8.boolean.opBoolean","SPLIT",EDGE,{"disambiguationData":[TD([makeQuery(id+"F5.opExtrude","SWEPT_FACE",FACE,{"disambiguationData":[OSD([sQuery(id+"F4.wireOp",EDGE,"E35.filletArc")])]})])],"derivedFrom":makeQuery(id+"F5.opExtrude","TWEAK_EDGE",EDGE,{"derivedFrom":[subQ0,makeQuery(id+"F4.imprint","IMPRINT",EDGE,{"derivedFrom":subQ1})]})});}
            var Q4;
            {var subQ0=sQuery(id+"F0.wireOp",EDGE,"E25.0");var subQ1=sQuery(id+"F0.wireOp",EDGE,"E25.1");var subQ2=sQuery(id+"F0.wireOp",EDGE,"E25.2");var subQ3=sQuery(id+"F0.wireOp",EDGE,"E25.3");var subQ4=sQuery(id+"F0.wireOp",EDGE,"E25.4");var subQ5=sQuery(id+"F0.wireOp",EDGE,"E25.5");var subQ6=sQuery(id+"F0.wireOp",EDGE,"E25.6");var subQ7=sQuery(id+"F0.wireOp",EDGE,"E25.7");Q4=makeQuery(id+"F8.boolean.opBoolean","INTERSECT",EDGE,{"derivedFrom":[makeQuery(id+"F5.boolean.opBoolean","SPLIT",FACE,{"disambiguationData":[TD([makeQuery(id+"F2.opExtrude","SWEPT_FACE",FACE,{"disambiguationData":[OSD([subQ0])]})])],"derivedFrom":makeQuery(id+"F3.boolean.opBoolean","COPY",FACE,{"derivedFrom":makeQuery(id+"F3.opExtrude","CAP_FACE",FACE,{"disambiguationData":[OSD([subQ0,subQ1,subQ2,subQ3,subQ4,subQ5,subQ6,subQ7])],"isStart":false})})}),makeQuery(id+"F8.opExtrude","SWEPT_FACE",FACE,{"disambiguationData":[OSD([sQuery(id+"F7.wireOp",EDGE,"E67")])]})]});}
            var Q5;
            Q5=makeQuery(id+"F8.boolean.opBoolean","INTERSECT",EDGE,{"disambiguationData":[OD(0.0)],"derivedFrom":[makeQuery(id+"F5.opExtrude","SWEPT_FACE",FACE,{"disambiguationData":[OSD([sQuery(id+"F4.wireOp",EDGE,"E30")])]}),makeQuery(id+"F8.opExtrude","SWEPT_FACE",FACE,{"disambiguationData":[OSD([sQuery(id+"F7.wireOp",EDGE,"E67")])]})]});
            fillet(context, id + "F14", {"entities" : qUnion([Q0, Q1, Q2, Q3, Q4, Q5]), "radius" : 3 * mm, "tangentPropagation" : true, "allowEdgeOverflow" : false});
        }
        {
            var Q0;
            Q0=makeQuery(id+"F1.opExtrude","CAP_EDGE",EDGE,{"disambiguationData":[OSD([sQuery(id+"F0.wireOp",EDGE,"E1.bottom")])],"isStart":false});
            fillet(context, id + "F15", {"entities" : qUnion([Q0]), "radius" : 2 * mm, "tangentPropagation" : true, "allowEdgeOverflow" : false});
        }
        {
            var Q0;
            {var subQ0=sQuery(id+"F0.wireOp",EDGE,"E21.filletArc");var subQ1=sQuery(id+"F0.wireOp",EDGE,"E7");var subQ2=sQuery(id+"F0.wireOp",EDGE,"E6");var subQ3=sQuery(id+"F0.wireOp",EDGE,"E5");var subQ4=sQuery(id+"F0.wireOp",EDGE,"E4");var subQ5=sQuery(id+"F0.wireOp",EDGE,"E22.filletArc");var subQ6=sQuery(id+"F0.wireOp",EDGE,"E1.bottom");var subQ7=sQuery(id+"F0.wireOp",EDGE,"E1.right");var subQ8=sQuery(id+"F0.wireOp",EDGE,"E1.top");var subQ9=sQuery(id+"F0.wireOp",EDGE,"E1.left");var subQ10=sQuery(id+"F0.wireOp",EDGE,"E23.filletArc");var subQ11=sQuery(id+"F0.wireOp",EDGE,"E24.filletArc");Q0=makeQuery(id+"F2.boolean.opBoolean","SPLIT",FACE,{"disambiguationData":[TD([makeQuery(id+"F1.opExtrude","SWEPT_FACE",FACE,{"disambiguationData":[OSD([subQ6])]})])],"derivedFrom":makeQuery(id+"F1.opExtrude","CAP_FACE",FACE,{"disambiguationData":[OSD([subQ6,subQ8,subQ9,subQ7,subQ4,subQ3,subQ2,subQ1,subQ0,subQ5,subQ10,subQ11])],"isStart":true})});}
            var sketch = newSketch(context, id + "F16", { "sketchPlane" : qUnion([Q0])});
            skLineSegment(sketch, "E79", {"start": v(0, 80) * mm, "end": v(0, 110) * mm, "construction": true});
            skCircle(sketch, "E80", {"center": v(0, 110) * mm, "radius": 6.96 * mm});
            skLineSegment(sketch, "E81", {"start": v(-33, 80) * mm, "end": v(-15, 98) * mm});
            skLineSegment(sketch, "E82", {"start": v(-15, 98) * mm, "end": v(-15, 110) * mm});
            skLineSegment(sketch, "E83", {"start": v(33, 80) * mm, "end": v(15, 92.25) * mm});
            skLineSegment(sketch, "E84", {"start": v(15, 92.25) * mm, "end": v(15, 110) * mm});
            skArc(sketch, "E85", {"start": v(15, 110) * mm, "mid": v(0, 125) * mm, "end": v(-15, 110) * mm});
            skLineSegment(sketch, "E86.MirrorCS", {"start": v(-33, -74.25) * mm, "end": v(-15, -92.25) * mm});
            skLineSegment(sketch, "E87.MirrorCS", {"start": v(0, -74.25) * mm, "end": v(0, -104.25) * mm, "construction": true});
            skCircle(sketch, "E88.MirrorC", {"center": v(0, -104.25) * mm, "radius": 6.96 * mm});
            skLineSegment(sketch, "E89.MirrorCS", {"start": v(-15, -92.25) * mm, "end": v(-15, -104.25) * mm});
            skLineSegment(sketch, "E90.MirrorCS", {"start": v(33, -74.25) * mm, "end": v(15, -92.25) * mm});
            skLineSegment(sketch, "E91.MirrorCS", {"start": v(15, -92.25) * mm, "end": v(15, -104.25) * mm});
            skArc(sketch, "E92.MirrorCS", {"start": v(15, -104.25) * mm, "mid": v(0, -119.25) * mm, "end": v(-15, -104.25) * mm});
            skSolve(sketch);
        }
        {
            var Q0;
            Q0=makeQuery(id+"F16.imprint","IMPRINT",FACE,{"disambiguationData":[TD([[makeQuery(id+"F16.imprint","IMPRINT",EDGE,{"derivedFrom":sQuery(id+"F16.wireOp",EDGE,"E80")}),-1.0]])]});
            var Q1;
            Q1=makeQuery(id+"F16.imprint","IMPRINT",FACE,{"disambiguationData":[TD([[makeQuery(id+"F16.imprint","IMPRINT",EDGE,{"derivedFrom":makeQuery(id+"F1.opExtrude","CAP_EDGE",EDGE,{"disambiguationData":[OSD([sQuery(id+"F0.wireOp",EDGE,"E1.left")])],"isStart":true})}),-1.0]])]});
            var Q2;
            {var subQ1=sQuery(id+"F16.wireOp",EDGE,"E86.MirrorCS");Q2=makeQuery(id+"F16.imprint","IMPRINT",FACE,{"disambiguationData":[TD([[makeQuery(id+"F16.imprint","IMPRINT",EDGE,{"derivedFrom":subQ1}),1.0]])]});}
            var Q3;
            Q3=makeQuery(id+"F2.opExtrude","CAP_FACE",FACE,{"disambiguationData":[OSD([sQuery(id+"F0.wireOp",EDGE,"E12"),sQuery(id+"F0.wireOp",EDGE,"E13"),sQuery(id+"F0.wireOp",EDGE,"E14"),sQuery(id+"F0.wireOp",EDGE,"E15"),sQuery(id+"F0.wireOp",EDGE,"E17.filletArc"),sQuery(id+"F0.wireOp",EDGE,"E18.filletArc"),sQuery(id+"F0.wireOp",EDGE,"E19.filletArc"),sQuery(id+"F0.wireOp",EDGE,"E20.filletArc"),sQuery(id+"F0.wireOp",EDGE,"E25.0"),sQuery(id+"F0.wireOp",EDGE,"E25.1"),sQuery(id+"F0.wireOp",EDGE,"E25.2"),sQuery(id+"F0.wireOp",EDGE,"E25.3"),sQuery(id+"F0.wireOp",EDGE,"E25.4"),sQuery(id+"F0.wireOp",EDGE,"E25.5"),sQuery(id+"F0.wireOp",EDGE,"E25.6"),sQuery(id+"F0.wireOp",EDGE,"E25.7")])],"isStart":false});
            extrude(context, id + "F17", {"entities" : qUnion([Q0, Q1, Q2]), "endBound" : BoundingType.UP_TO_SURFACE, "endBoundEntityFace" : qUnion([Q3]), "depth" : 25 * mm});
        }
    });
